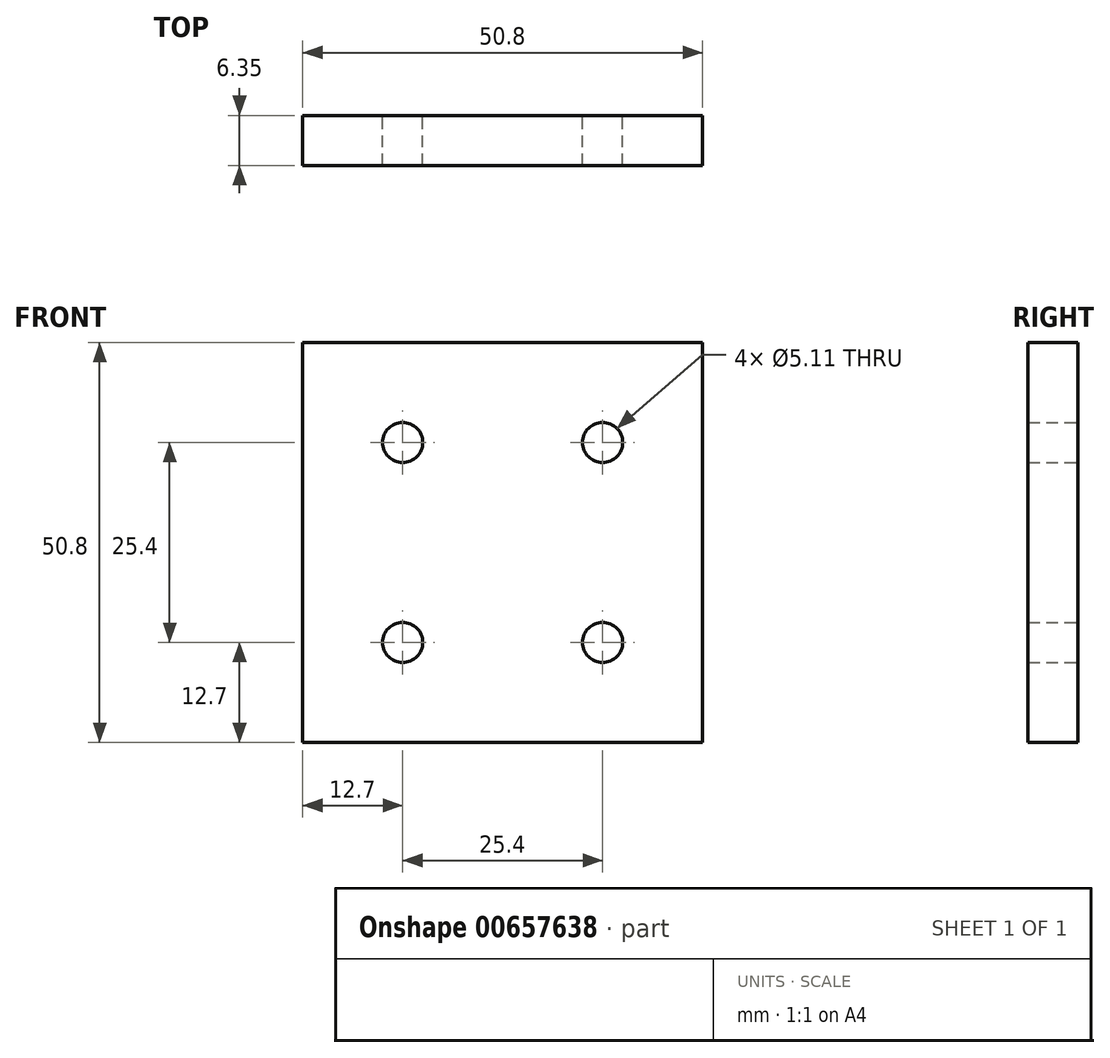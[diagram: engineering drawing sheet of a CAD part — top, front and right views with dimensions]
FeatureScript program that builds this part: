
annotation { "Feature Type Name" : "Feature", "Feature Type Description" : "" }
export const myFeature = defineFeature(function(context is Context, id is Id, definition is map)
    precondition{}
    {
        {
            var Q0;
            Q0=qCreatedBy(makeId("Front.planeOp"),FACE);
            var sketch = newSketch(context, id + "F0", { "sketchPlane" : qUnion([Q0])});
            skLineSegment(sketch, "E0.bottom", {"start": v(0, 0) * mm, "end": v(50.8, 0) * mm});
            skLineSegment(sketch, "E0.top", {"start": v(0, 50.8) * mm, "end": v(50.8, 50.8) * mm});
            skLineSegment(sketch, "E0.left", {"start": v(0, 0) * mm, "end": v(0, 50.8) * mm});
            skLineSegment(sketch, "E0.right", {"start": v(50.8, 0) * mm, "end": v(50.8, 50.8) * mm});
            skCircle(sketch, "E1", {"center": v(12.7, 38.1) * mm, "radius": 2.55 * mm});
            skCircle(sketch, "E2.0.1.0", {"center": v(12.7, 12.7) * mm, "radius": 2.55 * mm});
            skCircle(sketch, "E2.1.0.0", {"center": v(38.1, 38.1) * mm, "radius": 2.55 * mm});
            skCircle(sketch, "E2.1.1.0", {"center": v(38.1, 12.7) * mm, "radius": 2.55 * mm});
            skLineSegment(sketch, "E2.direction1", {"start": v(12.7, 38.1) * mm, "end": v(38.1, 38.1) * mm, "construction": true});
            skLineSegment(sketch, "E2.direction2", {"start": v(12.7, 38.1) * mm, "end": v(12.7, 12.7) * mm, "construction": true});
            skSolve(sketch);
        }
        {
            var Q0;
            Q0=makeQuery(id+"F0.imprint","IMPRINT",FACE,{"disambiguationData":[TD([[makeQuery(id+"F0.imprint","IMPRINT",EDGE,{"derivedFrom":sQuery(id+"F0.wireOp",EDGE,"E0.bottom")}),1.0]])]});
            extrude(context, id + "F1", {"entities" : qUnion([Q0]), "depth" : 6.35 * mm, "offsetDistance" : 25.4 * mm});
        }
    });
